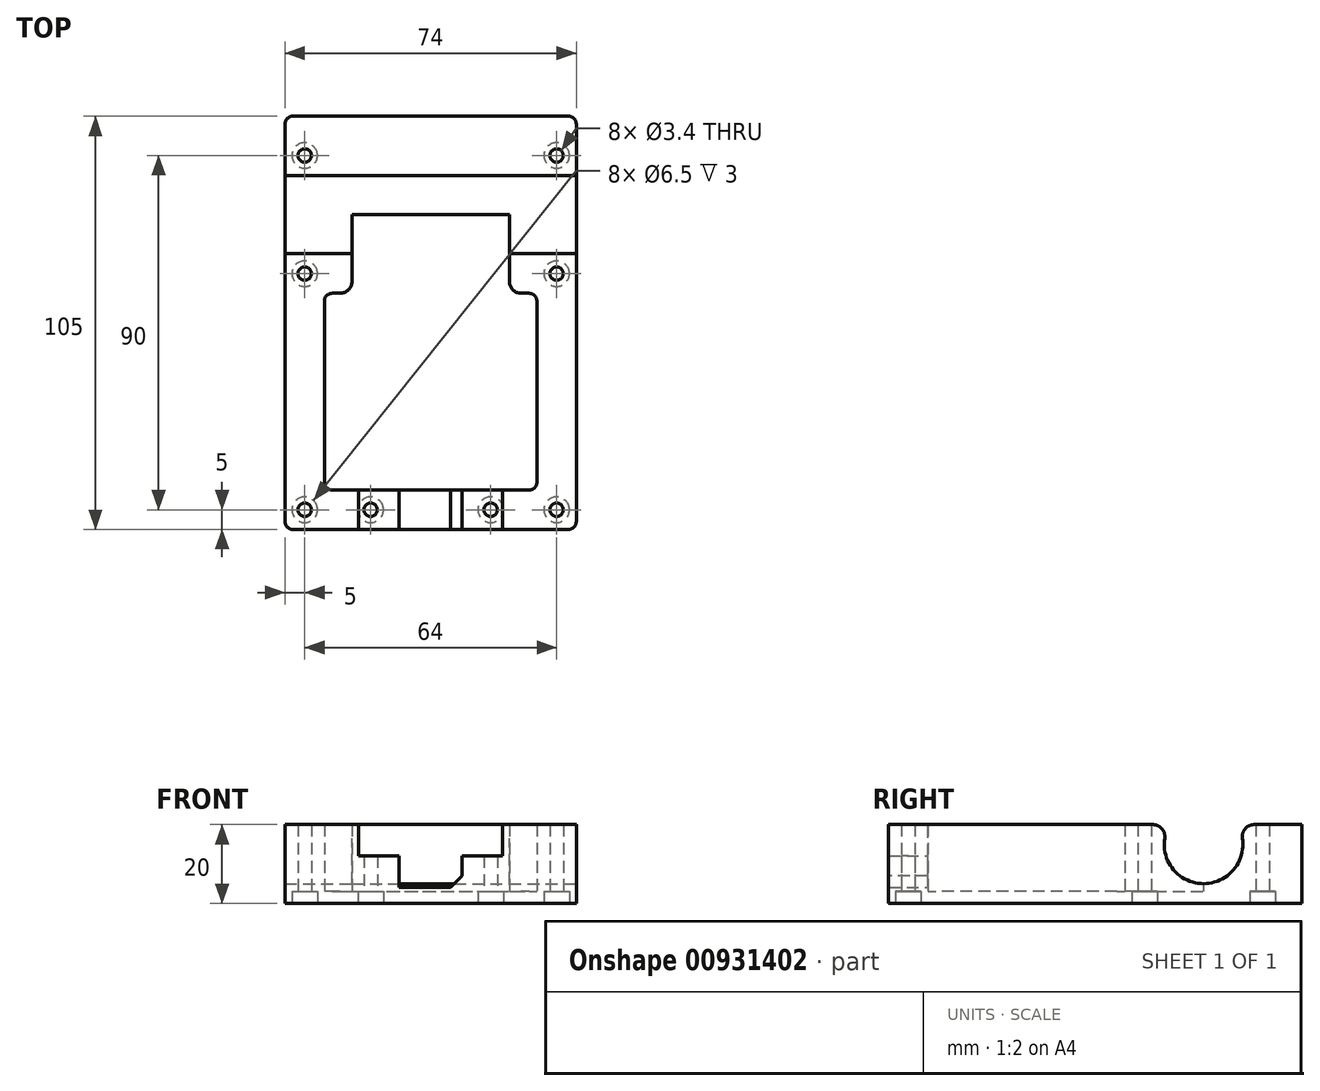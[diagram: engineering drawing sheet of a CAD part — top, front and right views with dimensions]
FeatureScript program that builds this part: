
annotation { "Feature Type Name" : "Feature", "Feature Type Description" : "" }
export const myFeature = defineFeature(function(context is Context, id is Id, definition is map)
    precondition{}
    {
        {
            var Q0;
            Q0=qCreatedBy(makeId("Top.planeOp"),FACE);
            var sketch = newSketch(context, id + "F0", { "sketchPlane" : qUnion([Q0])});
            skLineSegment(sketch, "E0.bottom", {"start": v(-37, 55) * mm, "end": v(37, 55) * mm});
            skLineSegment(sketch, "E0.top", {"start": v(-37, -50) * mm, "end": v(37, -50) * mm});
            skLineSegment(sketch, "E0.left", {"start": v(-37, 55) * mm, "end": v(-37, -50) * mm});
            skLineSegment(sketch, "E0.right", {"start": v(37, 55) * mm, "end": v(37, -50) * mm});
            skPoint(sketch, "E0.middle", {"position": v(0, 0) * mm});
            skSolve(sketch);
        }
        {
            var Q0;
            Q0=makeQuery(id+"F0.imprint","IMPRINT",FACE,{"disambiguationData":[TD([[makeQuery(id+"F0.imprint","IMPRINT",EDGE,{"derivedFrom":sQuery(id+"F0.wireOp",EDGE,"E0.bottom")}),-1.0]])]});
            var sketch = newSketch(context, id + "F1", { "sketchPlane" : qUnion([Q0])});
            skSolve(sketch);
        }
        {
            var Q0;
            Q0=makeQuery(id+"F1.imprint","IMPRINT",FACE,{"disambiguationData":[TD([[makeQuery(id+"F1.imprint","IMPRINT",EDGE,{"derivedFrom":makeQuery(id+"F0.imprint","IMPRINT",EDGE,{"derivedFrom":sQuery(id+"F0.wireOp",EDGE,"E0.bottom")})}),-1.0]])]});
            extrude(context, id + "F2", {"entities" : qUnion([Q0]), "depth" : 3 * mm, "offsetDistance" : 25 * mm});
        }
        {
            var Q0;
            Q0=makeQuery(id+"F2.opExtrude","CAP_FACE",FACE,{"disambiguationData":[OSD([sQuery(id+"F0.wireOp",EDGE,"E0.bottom"),sQuery(id+"F0.wireOp",EDGE,"E0.top"),sQuery(id+"F0.wireOp",EDGE,"E0.left"),sQuery(id+"F0.wireOp",EDGE,"E0.right")])],"isStart":false});
            var sketch = newSketch(context, id + "F3", { "sketchPlane" : qUnion([Q0])});
            skLineSegment(sketch, "E1.0", {"start": v(27, 10) * mm, "end": v(27, -40) * mm});
            skLineSegment(sketch, "E1.2", {"start": v(-27, 10) * mm, "end": v(-27, -40) * mm});
            skLineSegment(sketch, "E1.3", {"start": v(-27, -40) * mm, "end": v(27, -40) * mm});
            skLineSegment(sketch, "E2", {"start": v(27, 10) * mm, "end": v(20, 10) * mm});
            skLineSegment(sketch, "E3.top", {"start": v(-20, 30) * mm, "end": v(20, 30) * mm});
            skLineSegment(sketch, "E3.left", {"start": v(-20, 10) * mm, "end": v(-20, 30) * mm});
            skLineSegment(sketch, "E3.right", {"start": v(20, 10) * mm, "end": v(20, 30) * mm});
            skLineSegment(sketch, "E4.trimOffspring", {"start": v(-20, 10) * mm, "end": v(-27, 10) * mm});
            skSolve(sketch);
        }
        {
            var Q0;
            Q0=makeQuery(id+"F3.imprint","IMPRINT",FACE,{"disambiguationData":[TD([[makeQuery(id+"F3.imprint","IMPRINT",EDGE,{"derivedFrom":sQuery(id+"F3.wireOp",EDGE,"E1.0")}),1.0]])]});
            extrude(context, id + "F4", {"entities" : qUnion([Q0]), "operationType" : NewBodyOperationType.ADD, "depth" : 17 * mm, "offsetDistance" : 25 * mm});
        }
        {
            var Q0;
            Q0=makeQuery(id+"F2.opExtrude","SWEPT_FACE",FACE,{"disambiguationData":[OSD([sQuery(id+"F0.wireOp",EDGE,"E0.right")])]});
            var sketch = newSketch(context, id + "F5", { "sketchPlane" : qUnion([Q0])});
            skCircle(sketch, "E5", {"center": v(30, 15) * mm, "radius": 10 * mm});
            skSolve(sketch);
        }
        {
            var Q0;
            Q0=qSketchRegion(id+"F5",true);
            extrude(context, id + "F6", {"entities" : qUnion([Q0]), "operationType" : NewBodyOperationType.REMOVE, "endBound" : BoundingType.THROUGH_ALL, "oppositeDirection" : true, "depth" : 25 * mm, "offsetDistance" : 25 * mm});
        }
        {
            var Q0;
            Q0=makeQuery(id+"F0.imprint","IMPRINT",FACE,{"disambiguationData":[TD([[makeQuery(id+"F0.imprint","IMPRINT",EDGE,{"derivedFrom":sQuery(id+"F0.wireOp",EDGE,"E0.bottom")}),-1.0]])]});
            var sketch = newSketch(context, id + "F7", { "sketchPlane" : qUnion([Q0])});
            skPoint(sketch, "E6", {"position": v(32, 45) * mm});
            skPoint(sketch, "E7", {"position": v(32, 15) * mm});
            skPoint(sketch, "E8", {"position": v(-32, 15) * mm});
            skPoint(sketch, "E9", {"position": v(-32, 45) * mm});
            skPoint(sketch, "E10", {"position": v(32, -45) * mm});
            skPoint(sketch, "E11", {"position": v(-32, -45) * mm});
            skPoint(sketch, "E12", {"position": v(-15.25, -45) * mm});
            skPoint(sketch, "E13", {"position": v(15.25, -45) * mm});
            skSolve(sketch);
        }
        {
            var Q0;
            Q0=sQuery(id+"F7.wireOp",VERTEX,"E7");
            var Q1;
            Q1=sQuery(id+"F7.wireOp",VERTEX,"E6");
            var Q2;
            Q2=sQuery(id+"F7.wireOp",VERTEX,"E9");
            var Q3;
            Q3=sQuery(id+"F7.wireOp",VERTEX,"E8");
            var Q4;
            Q4=sQuery(id+"F7.wireOp",VERTEX,"E10");
            var Q5;
            Q5=sQuery(id+"F7.wireOp",VERTEX,"E11");
            var Q6;
            Q6=sQuery(id+"F7.wireOp",VERTEX,"E12");
            var Q7;
            Q7=sQuery(id+"F7.wireOp",VERTEX,"E13");
            var Q8;
            Q8=makeQuery(id+"F2.opExtrude","SWEPT_BODY",BODY,{"disambiguationData":[OSD([sQuery(id+"F0.wireOp",EDGE,"E0.bottom"),sQuery(id+"F0.wireOp",EDGE,"E0.top"),sQuery(id+"F0.wireOp",EDGE,"E0.left"),sQuery(id+"F0.wireOp",EDGE,"E0.right")])]});
            hole(context, id + "F8", {"style" : HoleStyle.C_BORE, "endStyle" : HoleEndStyle.THROUGH, "oppositeDirection" : true, "standardTappedOrClearance" : lookupTablePath({ "fit" : "Normal", "standard" : "ISO", "size" : "M3", "type" : "Clearance" }), "standardBlindInLast" : lookupTablePath({ "fit" : "Normal", "standard" : "ISO", "engagement" : "75%", "pitch" : "0.5 mm", "size" : "M3", "type" : "Clearance & tapped" }), "holeDiameter" : 3.4 * mm, "cBoreDiameter" : 6.5 * mm, "cBoreDepth" : 3 * mm, "majorDiameter" : 5 * mm, "isTappedThrough" : true, "tappedDepth" : 12 * mm, "tapClearance" : 3, "locations" : qUnion([Q0, Q1, Q2, Q3, Q4, Q5, Q6, Q7]), "scope" : qUnion([Q8])});
        }
        {
            var Q0;
            Q0=makeQuery(id+"F2.opExtrude","SWEPT_EDGE",EDGE,{"disambiguationData":[OSD([sQuery(id+"F0.wireOp",EDGE,"E0.bottom"),sQuery(id+"F0.wireOp",EDGE,"E0.right")])]});
            var Q1;
            Q1=makeQuery(id+"F2.opExtrude","SWEPT_EDGE",EDGE,{"disambiguationData":[OSD([sQuery(id+"F0.wireOp",EDGE,"E0.bottom"),sQuery(id+"F0.wireOp",EDGE,"E0.left")])]});
            var Q2;
            Q2=makeQuery(id+"F2.opExtrude","SWEPT_EDGE",EDGE,{"disambiguationData":[OSD([sQuery(id+"F0.wireOp",EDGE,"E0.top"),sQuery(id+"F0.wireOp",EDGE,"E0.right")])]});
            var Q3;
            Q3=makeQuery(id+"F2.opExtrude","SWEPT_EDGE",EDGE,{"disambiguationData":[OSD([sQuery(id+"F0.wireOp",EDGE,"E0.top"),sQuery(id+"F0.wireOp",EDGE,"E0.left")])]});
            fillet(context, id + "F9", {"entities" : qUnion([Q0, Q1, Q2, Q3]), "radius" : 2 * mm, "tangentPropagation" : true, "allowEdgeOverflow" : false});
        }
        {
            var Q0;
            Q0=makeQuery(id+"F4.opExtrude","SWEPT_EDGE",EDGE,{"disambiguationData":[OSD([sQuery(id+"F3.wireOp",EDGE,"E3.left"),sQuery(id+"F3.wireOp",EDGE,"E4.trimOffspring")])]});
            var Q1;
            Q1=makeQuery(id+"F4.opExtrude","SWEPT_EDGE",EDGE,{"disambiguationData":[OSD([sQuery(id+"F3.wireOp",EDGE,"E2"),sQuery(id+"F3.wireOp",EDGE,"E3.right")])]});
            fillet(context, id + "F10", {"entities" : qUnion([Q0, Q1]), "radius" : 3 * mm, "tangentPropagation" : true, "allowEdgeOverflow" : false});
        }
        {
            var Q0;
            Q0=makeQuery(id+"F4.opExtrude","SWEPT_EDGE",EDGE,{"disambiguationData":[OSD([sQuery(id+"F3.wireOp",EDGE,"E1.0"),sQuery(id+"F3.wireOp",EDGE,"E2")])]});
            var Q1;
            Q1=makeQuery(id+"F4.opExtrude","SWEPT_EDGE",EDGE,{"disambiguationData":[OSD([sQuery(id+"F3.wireOp",EDGE,"E1.2"),sQuery(id+"F3.wireOp",EDGE,"E4.trimOffspring")])]});
            var Q2;
            Q2=makeQuery(id+"F4.opExtrude","SWEPT_EDGE",EDGE,{"disambiguationData":[OSD([sQuery(id+"F3.wireOp",EDGE,"E1.2"),sQuery(id+"F3.wireOp",EDGE,"E1.3")])]});
            var Q3;
            Q3=makeQuery(id+"F4.opExtrude","SWEPT_EDGE",EDGE,{"disambiguationData":[OSD([sQuery(id+"F3.wireOp",EDGE,"E1.0"),sQuery(id+"F3.wireOp",EDGE,"E1.3")])]});
            fillet(context, id + "F11", {"entities" : qUnion([Q0, Q1, Q2, Q3]), "radius" : 2 * mm, "tangentPropagation" : true, "allowEdgeOverflow" : false});
        }
        {
            var Q0;
            {var subQ0=sQuery(id+"F3.wireOp",EDGE,"E4.trimOffspring");var subQ1=sQuery(id+"F3.wireOp",EDGE,"E3.right");var subQ2=sQuery(id+"F3.wireOp",EDGE,"E3.left");var subQ3=sQuery(id+"F3.wireOp",EDGE,"E2");var subQ4=sQuery(id+"F0.wireOp",EDGE,"E0.top");var subQ5=sQuery(id+"F3.wireOp",EDGE,"E1.0");var subQ6=sQuery(id+"F0.wireOp",EDGE,"E0.left");var subQ7=sQuery(id+"F3.wireOp",EDGE,"E1.2");var subQ8=sQuery(id+"F3.wireOp",EDGE,"E1.3");var subQ9=sQuery(id+"F0.wireOp",EDGE,"E0.right");Q0=makeQuery(id+"F6.boolean.opBoolean","SPLIT",FACE,{"disambiguationData":[TD([makeQuery(id+"F2.opExtrude","SWEPT_FACE",FACE,{"disambiguationData":[OSD([subQ4])]})])],"derivedFrom":makeQuery(id+"F4.opExtrude","CAP_FACE",FACE,{"disambiguationData":[OSD([sQuery(id+"F0.wireOp",EDGE,"E0.bottom"),subQ4,subQ6,subQ9,subQ5,subQ7,subQ8,subQ3,sQuery(id+"F3.wireOp",EDGE,"E3.top"),subQ2,subQ1,subQ0])],"isStart":false})});}
            var sketch = newSketch(context, id + "F12", { "sketchPlane" : qUnion([Q0])});
            skLineSegment(sketch, "E14.bottom", {"start": v(-18.25, -50) * mm, "end": v(18.25, -50) * mm});
            skLineSegment(sketch, "E14.top", {"start": v(-18.25, -40) * mm, "end": v(18.25, -40) * mm});
            skLineSegment(sketch, "E14.left", {"start": v(-18.25, -50) * mm, "end": v(-18.25, -40) * mm});
            skLineSegment(sketch, "E14.right", {"start": v(18.25, -50) * mm, "end": v(18.25, -40) * mm});
            skSolve(sketch);
        }
        {
            var Q0;
            Q0=makeQuery(id+"F12.imprint","IMPRINT",FACE,{"disambiguationData":[TD([[makeQuery(id+"F12.imprint","IMPRINT",EDGE,{"derivedFrom":sQuery(id+"F12.wireOp",EDGE,"E14.bottom")}),1.0]])]});
            extrude(context, id + "F13", {"entities" : qUnion([Q0]), "operationType" : NewBodyOperationType.REMOVE, "oppositeDirection" : true, "depth" : 8 * mm, "offsetDistance" : 25 * mm});
        }
        {
            var Q0;
            {var subQ0=sQuery(id+"F3.wireOp",EDGE,"E4.trimOffspring");var subQ1=sQuery(id+"F3.wireOp",EDGE,"E3.right");var subQ2=sQuery(id+"F3.wireOp",EDGE,"E3.left");var subQ3=sQuery(id+"F3.wireOp",EDGE,"E2");var subQ4=sQuery(id+"F0.wireOp",EDGE,"E0.top");var subQ5=sQuery(id+"F3.wireOp",EDGE,"E1.0");var subQ6=sQuery(id+"F0.wireOp",EDGE,"E0.left");var subQ7=sQuery(id+"F3.wireOp",EDGE,"E1.2");var subQ8=sQuery(id+"F3.wireOp",EDGE,"E1.3");var subQ9=sQuery(id+"F0.wireOp",EDGE,"E0.right");Q0=makeQuery(id+"F6.boolean.opBoolean","SPLIT",FACE,{"disambiguationData":[TD([makeQuery(id+"F2.opExtrude","SWEPT_FACE",FACE,{"disambiguationData":[OSD([subQ4])]})])],"derivedFrom":makeQuery(id+"F4.opExtrude","CAP_FACE",FACE,{"disambiguationData":[OSD([sQuery(id+"F0.wireOp",EDGE,"E0.bottom"),subQ4,subQ6,subQ9,subQ5,subQ7,subQ8,subQ3,sQuery(id+"F3.wireOp",EDGE,"E3.top"),subQ2,subQ1,subQ0])],"isStart":false})});}
            var sketch = newSketch(context, id + "F14", { "sketchPlane" : qUnion([Q0])});
            skLineSegment(sketch, "E15.bottom", {"start": v(-8, -50) * mm, "end": v(8, -50) * mm});
            skLineSegment(sketch, "E15.top", {"start": v(-8, -40) * mm, "end": v(8, -40) * mm});
            skLineSegment(sketch, "E15.left", {"start": v(-8, -50) * mm, "end": v(-8, -40) * mm});
            skLineSegment(sketch, "E15.right", {"start": v(8, -50) * mm, "end": v(8, -40) * mm});
            skSolve(sketch);
        }
        {
            var Q0;
            Q0=makeQuery(id+"F14.imprint","IMPRINT",FACE,{"disambiguationData":[TD([[makeQuery(id+"F14.imprint","IMPRINT",EDGE,{"derivedFrom":sQuery(id+"F14.wireOp",EDGE,"E15.bottom")}),1.0]])]});
            extrude(context, id + "F15", {"entities" : qUnion([Q0]), "operationType" : NewBodyOperationType.REMOVE, "oppositeDirection" : true, "depth" : 16 * mm, "offsetDistance" : 25 * mm});
        }
        {
            var Q0;
            Q0=makeQuery(id+"F15.boolean.opBoolean","COPY",EDGE,{"derivedFrom":makeQuery(id+"F15.opExtrude","CAP_EDGE",EDGE,{"disambiguationData":[OSD([sQuery(id+"F14.wireOp",EDGE,"E15.right")])],"isStart":false})});
            chamfer(context, id + "F16", {"entities" : qUnion([Q0]), "width" : 3 * mm, "tangentPropagation" : true});
        }
        {
            var Q0;
            Q0=makeQuery(id+"F6.boolean.opBoolean","INTERSECT",EDGE,{"disambiguationData":[OD(0.0)],"derivedFrom":[makeQuery(id+"F4.opExtrude","CAP_FACE",FACE,{"disambiguationData":[OSD([sQuery(id+"F0.wireOp",EDGE,"E0.bottom"),sQuery(id+"F0.wireOp",EDGE,"E0.top"),sQuery(id+"F0.wireOp",EDGE,"E0.left"),sQuery(id+"F0.wireOp",EDGE,"E0.right"),sQuery(id+"F3.wireOp",EDGE,"E1.0"),sQuery(id+"F3.wireOp",EDGE,"E1.2"),sQuery(id+"F3.wireOp",EDGE,"E1.3"),sQuery(id+"F3.wireOp",EDGE,"E2"),sQuery(id+"F3.wireOp",EDGE,"E3.top"),sQuery(id+"F3.wireOp",EDGE,"E3.left"),sQuery(id+"F3.wireOp",EDGE,"E3.right"),sQuery(id+"F3.wireOp",EDGE,"E4.trimOffspring")])],"isStart":false}),makeQuery(id+"F6.opExtrude","SWEPT_FACE",FACE,{"disambiguationData":[OSD([sQuery(id+"F5.wireOp",EDGE,"E5")])]})]});
            var Q1;
            Q1=makeQuery(id+"F6.boolean.opBoolean","INTERSECT",EDGE,{"disambiguationData":[OD(1.0)],"derivedFrom":[makeQuery(id+"F4.opExtrude","CAP_FACE",FACE,{"disambiguationData":[OSD([sQuery(id+"F0.wireOp",EDGE,"E0.bottom"),sQuery(id+"F0.wireOp",EDGE,"E0.top"),sQuery(id+"F0.wireOp",EDGE,"E0.left"),sQuery(id+"F0.wireOp",EDGE,"E0.right"),sQuery(id+"F3.wireOp",EDGE,"E1.0"),sQuery(id+"F3.wireOp",EDGE,"E1.2"),sQuery(id+"F3.wireOp",EDGE,"E1.3"),sQuery(id+"F3.wireOp",EDGE,"E2"),sQuery(id+"F3.wireOp",EDGE,"E3.top"),sQuery(id+"F3.wireOp",EDGE,"E3.left"),sQuery(id+"F3.wireOp",EDGE,"E3.right"),sQuery(id+"F3.wireOp",EDGE,"E4.trimOffspring")])],"isStart":false}),makeQuery(id+"F6.opExtrude","SWEPT_FACE",FACE,{"disambiguationData":[OSD([sQuery(id+"F5.wireOp",EDGE,"E5")])]})]});
            var Q2;
            Q2=makeQuery(id+"F6.boolean.opBoolean","INTERSECT",EDGE,{"disambiguationData":[OD(2.0)],"derivedFrom":[makeQuery(id+"F4.opExtrude","CAP_FACE",FACE,{"disambiguationData":[OSD([sQuery(id+"F0.wireOp",EDGE,"E0.bottom"),sQuery(id+"F0.wireOp",EDGE,"E0.top"),sQuery(id+"F0.wireOp",EDGE,"E0.left"),sQuery(id+"F0.wireOp",EDGE,"E0.right"),sQuery(id+"F3.wireOp",EDGE,"E1.0"),sQuery(id+"F3.wireOp",EDGE,"E1.2"),sQuery(id+"F3.wireOp",EDGE,"E1.3"),sQuery(id+"F3.wireOp",EDGE,"E2"),sQuery(id+"F3.wireOp",EDGE,"E3.top"),sQuery(id+"F3.wireOp",EDGE,"E3.left"),sQuery(id+"F3.wireOp",EDGE,"E3.right"),sQuery(id+"F3.wireOp",EDGE,"E4.trimOffspring")])],"isStart":false}),makeQuery(id+"F6.opExtrude","SWEPT_FACE",FACE,{"disambiguationData":[OSD([sQuery(id+"F5.wireOp",EDGE,"E5")])]})]});
            fillet(context, id + "F17", {"entities" : qUnion([Q0, Q1, Q2]), "radius" : 3 * mm, "tangentPropagation" : true, "allowEdgeOverflow" : false});
        }
    });
